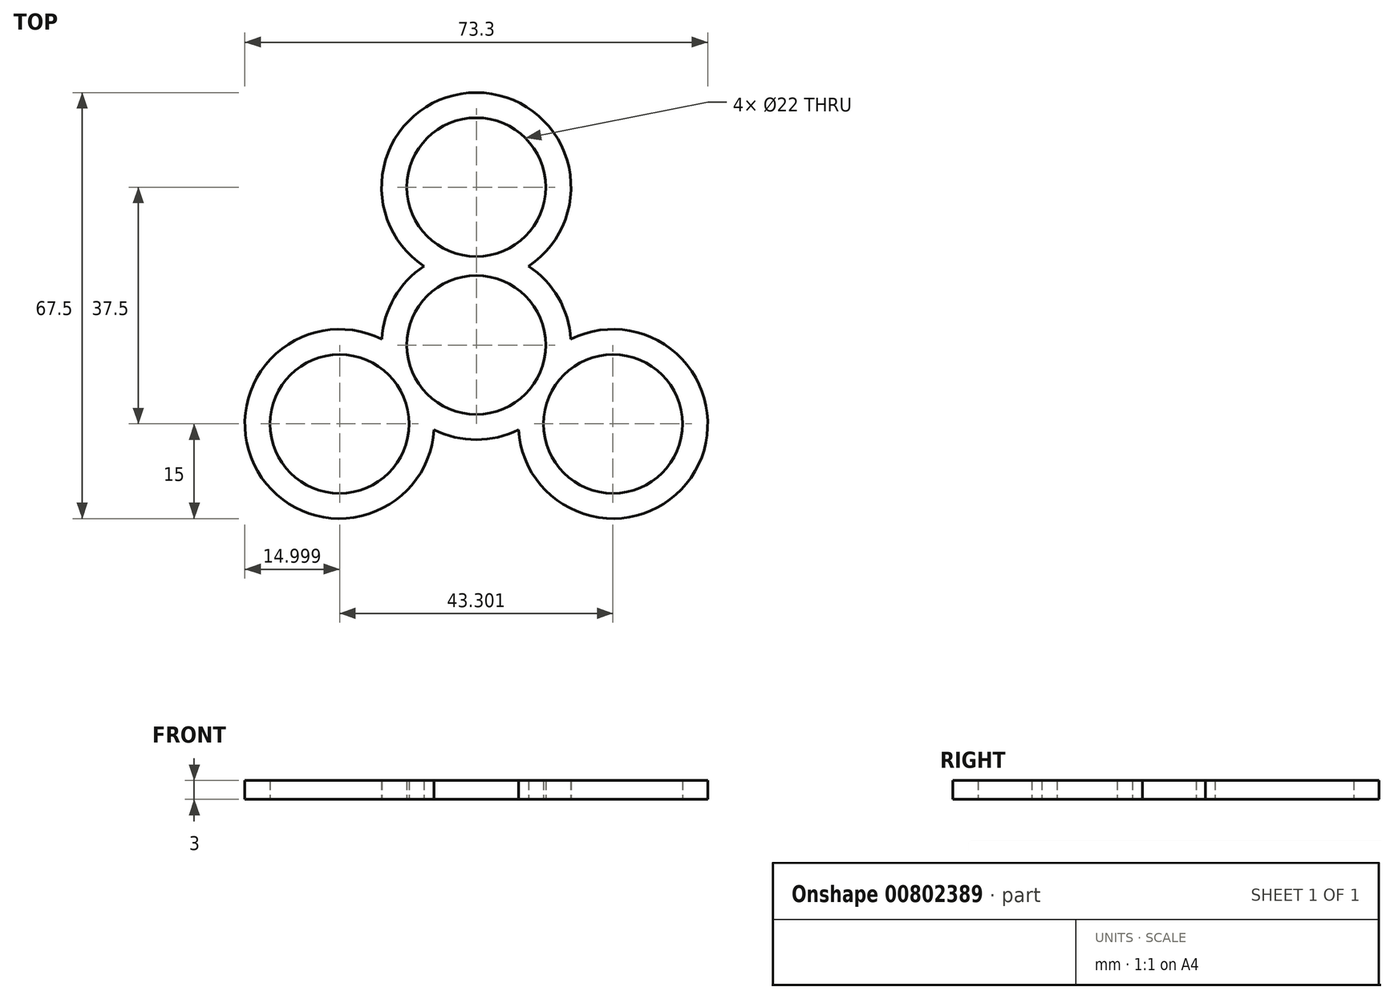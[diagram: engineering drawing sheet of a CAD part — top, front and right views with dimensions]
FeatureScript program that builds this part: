
annotation { "Feature Type Name" : "Feature", "Feature Type Description" : "" }
export const myFeature = defineFeature(function(context is Context, id is Id, definition is map)
    precondition{}
    {
        {
            var Q0;
            Q0=qCreatedBy(makeId("Top.planeOp"),FACE);
            var sketch = newSketch(context, id + "F0", { "sketchPlane" : qUnion([Q0])});
            skArc(sketch, "E0", {"start": v(9.53, 5.5) * mm, "mid": v(0, 11) * mm, "end": v(-9.53, 5.5) * mm});
            skLineSegment(sketch, "E1", {"start": v(0, 0) * mm, "end": v(0, 11) * mm});
            skCircle(sketch, "E2", {"center": v(0, 25) * mm, "radius": 11 * mm});
            skArc(sketch, "E3", {"start": v(-8.3, 12.5) * mm, "mid": v(-10.93, 10.27) * mm, "end": v(-13, 7.5) * mm});
            skArc(sketch, "E4", {"start": v(8.3, 12.5) * mm, "mid": v(0, 40) * mm, "end": v(-8.3, 12.5) * mm});
            skArc(sketch, "E5.trimOffspring", {"start": v(13, 7.5) * mm, "mid": v(10.93, 10.27) * mm, "end": v(8.3, 12.5) * mm});
            skArc(sketch, "E6.1.0", {"start": v(-14.97, 0.93) * mm, "mid": v(-34.64, -20) * mm, "end": v(-6.68, -13.43) * mm});
            skCircle(sketch, "E6.1.1", {"center": v(-21.65, -12.5) * mm, "radius": 11 * mm});
            skArc(sketch, "E6.1.2", {"start": v(-6.68, -13.43) * mm, "mid": v(-3.43, -14.6) * mm, "end": v(0, -15) * mm});
            skArc(sketch, "E6.1.3", {"start": v(-9.53, 5.5) * mm, "mid": v(-9.53, -5.5) * mm, "end": v(0, -11) * mm});
            skArc(sketch, "E6.1.4", {"start": v(-13, 7.5) * mm, "mid": v(-14.36, 4.33) * mm, "end": v(-14.97, 0.93) * mm});
            skArc(sketch, "E6.2.0", {"start": v(6.68, -13.43) * mm, "mid": v(34.64, -20) * mm, "end": v(14.97, 0.93) * mm});
            skCircle(sketch, "E6.2.1", {"center": v(21.65, -12.5) * mm, "radius": 11 * mm});
            skArc(sketch, "E6.2.2", {"start": v(14.97, 0.93) * mm, "mid": v(14.36, 4.33) * mm, "end": v(13, 7.5) * mm});
            skArc(sketch, "E6.2.3", {"start": v(0, -11) * mm, "mid": v(9.53, -5.5) * mm, "end": v(9.53, 5.5) * mm});
            skArc(sketch, "E6.2.4", {"start": v(0, -15) * mm, "mid": v(3.43, -14.6) * mm, "end": v(6.68, -13.43) * mm});
            skSolve(sketch);
        }
        {
            var Q0;
            Q0 = qSketchRegion(id + "F0", true);
            extrude(context, id + "F1", {"entities" : qUnion([Q0]), "depth" : 3 * mm, "offsetDistance" : 25 * mm});
        }
    });
